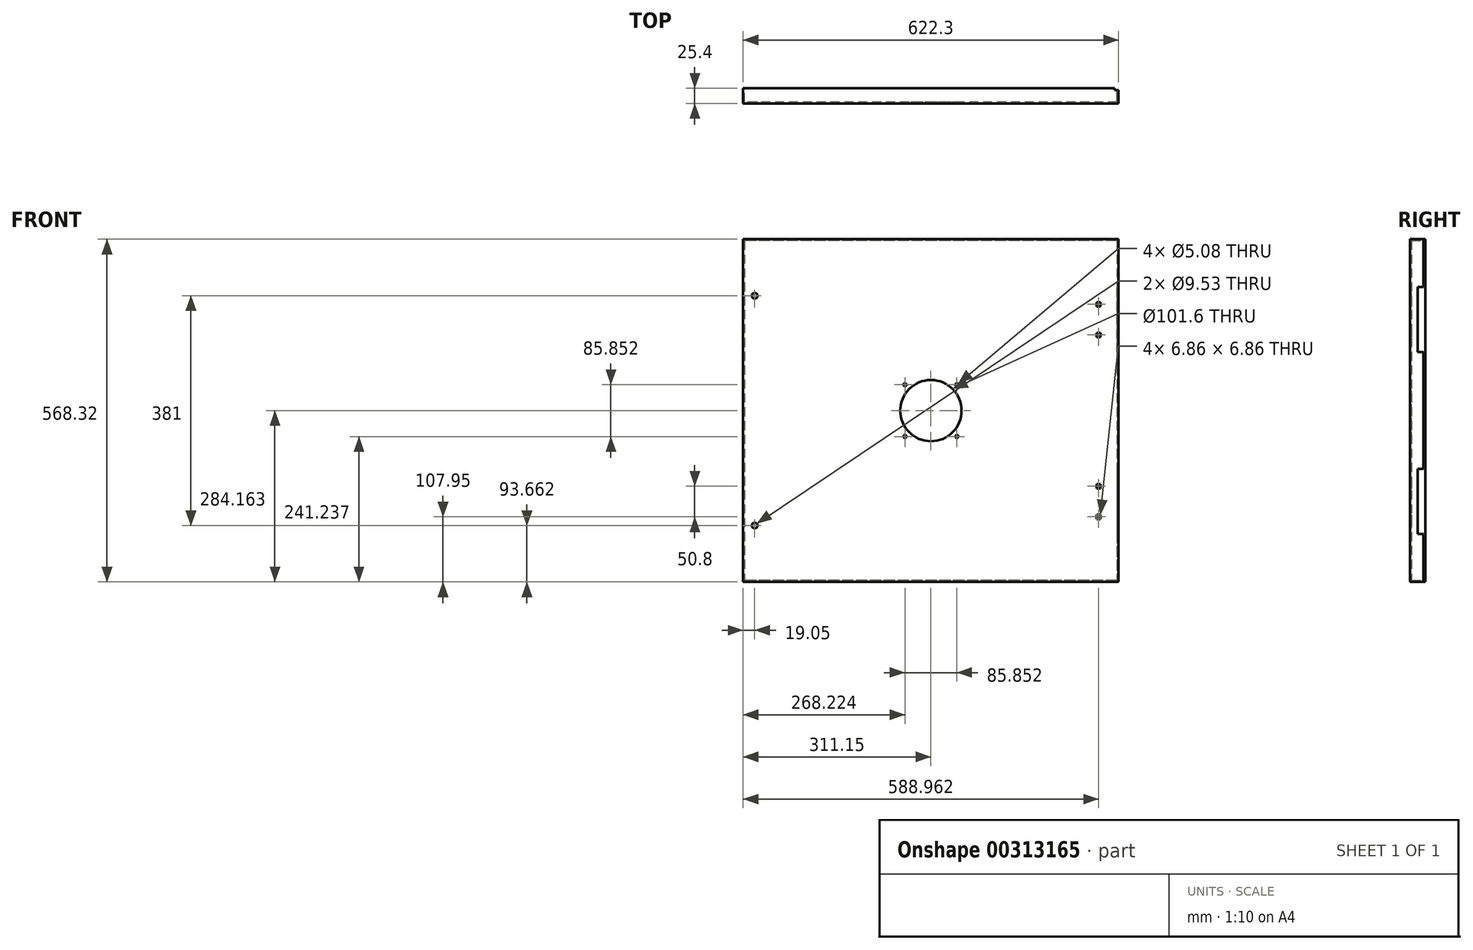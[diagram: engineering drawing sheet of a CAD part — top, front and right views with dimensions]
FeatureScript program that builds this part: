
annotation { "Feature Type Name" : "Feature", "Feature Type Description" : "" }
export const myFeature = defineFeature(function(context is Context, id is Id, definition is map)
    precondition{}
    {
        {
            var Q0;
            Q0=qCreatedBy(makeId("Front.planeOp"),FACE);
            var sketch = newSketch(context, id + "F0", { "sketchPlane" : qUnion([Q0])});
            skLineSegment(sketch, "E0.bottom", {"start": v(311.15, 568.33) * mm, "end": v(-311.15, 568.33) * mm});
            skLineSegment(sketch, "E0.top", {"start": v(311.15, 0) * mm, "end": v(-311.15, 0) * mm});
            skLineSegment(sketch, "E0.left", {"start": v(311.15, 568.32) * mm, "end": v(311.15, 0) * mm});
            skLineSegment(sketch, "E0.right", {"start": v(-311.15, 568.32) * mm, "end": v(-311.15, 0) * mm});
            skCircle(sketch, "E1", {"center": v(-292.1, 474.66) * mm, "radius": 4.76 * mm});
            skCircle(sketch, "E2", {"center": v(-292.1, 93.66) * mm, "radius": 4.76 * mm});
            skCircle(sketch, "E3", {"center": v(277.81, 460.38) * mm, "radius": 3.18 * mm, "construction": true});
            skCircle(sketch, "E4", {"center": v(277.81, 409.58) * mm, "radius": 3.18 * mm, "construction": true});
            skCircle(sketch, "E5", {"center": v(277.81, 158.75) * mm, "radius": 3.18 * mm, "construction": true});
            skCircle(sketch, "E6", {"center": v(277.81, 107.95) * mm, "radius": 3.18 * mm, "construction": true});
            skCircle(sketch, "E7", {"center": v(0, 284.16) * mm, "radius": 50.8 * mm});
            skPoint(sketch, "E7.centerSnap0", {"position": v(-311.15, 284.16) * mm});
            skPoint(sketch, "E7.centerSnap1", {"position": v(0, 568.32) * mm});
            skCircle(sketch, "E8", {"center": v(42.93, 327.09) * mm, "radius": 2.54 * mm});
            skCircle(sketch, "E9", {"center": v(-42.93, 327.09) * mm, "radius": 2.54 * mm});
            skCircle(sketch, "E10", {"center": v(-42.93, 241.24) * mm, "radius": 2.54 * mm});
            skCircle(sketch, "E11", {"center": v(42.93, 241.24) * mm, "radius": 2.54 * mm});
            skLineSegment(sketch, "E12.bottom", {"start": v(281.24, 463.8) * mm, "end": v(274.38, 463.8) * mm});
            skLineSegment(sketch, "E12.top", {"start": v(281.24, 456.95) * mm, "end": v(274.38, 456.95) * mm});
            skLineSegment(sketch, "E12.left", {"start": v(281.24, 463.8) * mm, "end": v(281.24, 456.95) * mm});
            skLineSegment(sketch, "E12.right", {"start": v(274.38, 463.8) * mm, "end": v(274.38, 456.95) * mm});
            skLineSegment(sketch, "E13.bottom", {"start": v(281.24, 413) * mm, "end": v(274.38, 413) * mm});
            skLineSegment(sketch, "E13.top", {"start": v(281.24, 406.15) * mm, "end": v(274.38, 406.15) * mm});
            skLineSegment(sketch, "E13.left", {"start": v(281.24, 413) * mm, "end": v(281.24, 406.15) * mm});
            skLineSegment(sketch, "E13.right", {"start": v(274.38, 413) * mm, "end": v(274.38, 406.15) * mm});
            skLineSegment(sketch, "E14.bottom", {"start": v(281.24, 162.18) * mm, "end": v(274.38, 162.18) * mm});
            skLineSegment(sketch, "E14.top", {"start": v(281.24, 155.32) * mm, "end": v(274.38, 155.32) * mm});
            skLineSegment(sketch, "E14.left", {"start": v(281.24, 162.18) * mm, "end": v(281.24, 155.32) * mm});
            skLineSegment(sketch, "E14.right", {"start": v(274.38, 162.18) * mm, "end": v(274.38, 155.32) * mm});
            skLineSegment(sketch, "E15.bottom", {"start": v(281.24, 111.38) * mm, "end": v(274.38, 111.38) * mm});
            skLineSegment(sketch, "E15.top", {"start": v(281.24, 104.52) * mm, "end": v(274.38, 104.52) * mm});
            skLineSegment(sketch, "E15.left", {"start": v(281.24, 111.38) * mm, "end": v(281.24, 104.52) * mm});
            skLineSegment(sketch, "E15.right", {"start": v(274.38, 111.38) * mm, "end": v(274.38, 104.52) * mm});
            skPoint(sketch, "E15.cornerSnap0", {"position": v(281.24, 158.75) * mm});
            skSolve(sketch);
        }
        {
            var Q0;
            Q0=qSketchRegion(id+"F0",true);
            extrude(context, id + "F1", {"entities" : qUnion([Q0]), "depth" : 25.4 * mm});
        }
        {
            var Q0;
            Q0=makeQuery(id+"F1.opExtrude","CAP_FACE",FACE,{"disambiguationData":[OSD([sQuery(id+"F0.wireOp",EDGE,"E0.bottom"),sQuery(id+"F0.wireOp",EDGE,"E0.top"),sQuery(id+"F0.wireOp",EDGE,"E0.left"),sQuery(id+"F0.wireOp",EDGE,"E0.right"),sQuery(id+"F0.wireOp",EDGE,"DnOeYdpL-yZhG-pMPP-nWlj-HbxDlVvFq81o.bottom"),sQuery(id+"F0.wireOp",EDGE,"DnOeYdpL-yZhG-pMPP-nWlj-HbxDlVvFq81o.top"),sQuery(id+"F0.wireOp",EDGE,"DnOeYdpL-yZhG-pMPP-nWlj-HbxDlVvFq81o.left"),sQuery(id+"F0.wireOp",EDGE,"DnOeYdpL-yZhG-pMPP-nWlj-HbxDlVvFq81o.right"),sQuery(id+"F0.wireOp",EDGE,"xDgMzqlZ-3YCT-1KnM-qA8u-792qYw5lw1JS"),sQuery(id+"F0.wireOp",EDGE,"Mpdr3xRK-0yTI-dkfT-nTdE-cEWg6RnXpa9N"),sQuery(id+"F0.wireOp",EDGE,"UzSud16w-tGWN-ZEeO-kTY7-zgmRVJxoJOe7"),sQuery(id+"F0.wireOp",EDGE,"QdRWkNVw-568D-XgAy-SO4V-4Q89nbcZrelq"),sQuery(id+"F0.wireOp",EDGE,"8aFPr5qc-bRuC-cZr7-87dc-hIFrfZXMsOHR"),sQuery(id+"F0.wireOp",EDGE,"mJVcAo0T-mOHa-Qb8O-DeX9-rnRp2EFAdPQ3"),sQuery(id+"F0.wireOp",EDGE,"58VjJvAl-gczf-lvPp-maZi-m7BX2DlegteS"),sQuery(id+"F0.wireOp",EDGE,"xgLxJu9m-eS83-UV5U-zqJ0-FrWtQ9vBuum0"),sQuery(id+"F0.wireOp",EDGE,"wqzXiebe-RaGP-8YjT-blUU-62aUiCvM27mv"),sQuery(id+"F0.wireOp",EDGE,"zmVhXP7j-02Ai-JLcr-0Ks7-3LBVpZUHfUrI"),sQuery(id+"F0.wireOp",EDGE,"BW3LuwXz-W35X-CTuh-aFvS-jlk6UlRIqyyT"),sQuery(id+"F0.wireOp",EDGE,"GNJOQj1j-LiCZ-vYCN-EfaB-cui9jyFQZn0N"),sQuery(id+"F0.wireOp",EDGE,"da7037a2-8101-4e2d-bd9b-c90a86b3fb6c.1.0.1"),sQuery(id+"F0.wireOp",EDGE,"da7037a2-8101-4e2d-bd9b-c90a86b3fb6c.1.0.2"),sQuery(id+"F0.wireOp",EDGE,"da7037a2-8101-4e2d-bd9b-c90a86b3fb6c.1.0.3"),sQuery(id+"F0.wireOp",EDGE,"da7037a2-8101-4e2d-bd9b-c90a86b3fb6c.1.0.4"),sQuery(id+"F0.wireOp",EDGE,"da7037a2-8101-4e2d-bd9b-c90a86b3fb6c.1.0.5"),sQuery(id+"F0.wireOp",EDGE,"da7037a2-8101-4e2d-bd9b-c90a86b3fb6c.1.0.6"),sQuery(id+"F0.wireOp",EDGE,"da7037a2-8101-4e2d-bd9b-c90a86b3fb6c.1.0.7"),sQuery(id+"F0.wireOp",EDGE,"da7037a2-8101-4e2d-bd9b-c90a86b3fb6c.1.0.8"),sQuery(id+"F0.wireOp",EDGE,"da7037a2-8101-4e2d-bd9b-c90a86b3fb6c.1.0.9"),sQuery(id+"F0.wireOp",EDGE,"da7037a2-8101-4e2d-bd9b-c90a86b3fb6c.1.0.10"),sQuery(id+"F0.wireOp",EDGE,"da7037a2-8101-4e2d-bd9b-c90a86b3fb6c.1.0.11"),sQuery(id+"F0.wireOp",EDGE,"da7037a2-8101-4e2d-bd9b-c90a86b3fb6c.1.0.12"),sQuery(id+"F0.wireOp",EDGE,"da7037a2-8101-4e2d-bd9b-c90a86b3fb6c.1.0.13"),sQuery(id+"F0.wireOp",EDGE,"da7037a2-8101-4e2d-bd9b-c90a86b3fb6c.1.0.14"),sQuery(id+"F0.wireOp",EDGE,"da7037a2-8101-4e2d-bd9b-c90a86b3fb6c.1.0.15"),sQuery(id+"F0.wireOp",EDGE,"da7037a2-8101-4e2d-bd9b-c90a86b3fb6c.1.0.16")])],"isStart":true});
            shell(context, id + "F2", {"entities" : qUnion([Q0]), "thickness" : 2.54 * mm});
        }
        {
            var Q0;
            Q0=makeQuery(id+"F2.opShell","OFFSET_FACE",FACE,{"disambiguationData":[OSD([sQuery(id+"F0.wireOp",EDGE,"E0.top")])]});
            var sketch = newSketch(context, id + "F3", { "sketchPlane" : qUnion([Q0])});
            skLineSegment(sketch, "E16.bottom", {"start": v(308.61, 0) * mm, "end": v(-308.61, 0) * mm});
            skLineSegment(sketch, "E16.top", {"start": v(308.61, -22.86) * mm, "end": v(-308.61, -22.86) * mm});
            skLineSegment(sketch, "E16.left", {"start": v(308.61, 0) * mm, "end": v(308.61, -22.86) * mm});
            skLineSegment(sketch, "E16.right", {"start": v(-308.61, 0) * mm, "end": v(-308.61, -22.86) * mm});
            skSolve(sketch);
        }
        {
            var Q0;
            Q0 = qSketchRegion(id + "F3", true);
            var Q1;
            Q1=makeQuery(id+"F2.opShell","OFFSET_FACE",FACE,{"disambiguationData":[OSD([sQuery(id+"F0.wireOp",EDGE,"E0.bottom")])]});
            extrude(context, id + "F4", {"entities" : qUnion([Q0]), "operationType" : NewBodyOperationType.REMOVE, "endBound" : BoundingType.UP_TO_SURFACE, "endBoundEntityFace" : qUnion([Q1]), "depth" : 25.4 * mm});
        }
        {
            var Q0;
            Q0=makeQuery(id+"F1.opExtrude","SWEPT_FACE",FACE,{"disambiguationData":[OSD([sQuery(id+"F0.wireOp",EDGE,"E0.bottom")])]});
            var sketch = newSketch(context, id + "F5", { "sketchPlane" : qUnion([Q0])});
            skLineSegment(sketch, "E17", {"start": v(304.8, 0) * mm, "end": v(304.8, -3.18) * mm});
            skLineSegment(sketch, "E18", {"start": v(304.8, -3.18) * mm, "end": v(311.15, -3.18) * mm});
            skLineSegment(sketch, "E19", {"start": v(311.15, -3.18) * mm, "end": v(311.15, 0) * mm});
            skLineSegment(sketch, "E20", {"start": v(304.8, 0) * mm, "end": v(311.15, 0) * mm});
            skSolve(sketch);
        }
        {
            var Q0;
            Q0 = qSketchRegion(id + "F5", true);
            extrude(context, id + "F6", {"entities" : qUnion([Q0]), "operationType" : NewBodyOperationType.REMOVE, "endBound" : BoundingType.THROUGH_ALL, "oppositeDirection" : true, "depth" : 25.4 * mm});
        }
        {
            var Q0;
            Q0=makeQuery(id+"F1.opExtrude","SWEPT_FACE",FACE,{"disambiguationData":[OSD([sQuery(id+"F0.wireOp",EDGE,"E0.left")])]});
            var sketch = newSketch(context, id + "F7", { "sketchPlane" : qUnion([Q0])});
            skLineSegment(sketch, "E21.bottom", {"start": v(0, 488.95) * mm, "end": v(-12.7, 488.95) * mm});
            skLineSegment(sketch, "E21.top", {"start": v(0, 381) * mm, "end": v(-12.7, 381) * mm});
            skLineSegment(sketch, "E21.left", {"start": v(0, 488.95) * mm, "end": v(0, 381) * mm});
            skLineSegment(sketch, "E21.right", {"start": v(-12.7, 488.95) * mm, "end": v(-12.7, 381) * mm});
            skLineSegment(sketch, "E22.bottom", {"start": v(0, 79.37) * mm, "end": v(-12.7, 79.37) * mm});
            skLineSegment(sketch, "E22.top", {"start": v(0, 187.32) * mm, "end": v(-12.7, 187.32) * mm});
            skLineSegment(sketch, "E22.left", {"start": v(0, 79.37) * mm, "end": v(0, 187.32) * mm});
            skLineSegment(sketch, "E22.right", {"start": v(-12.7, 79.37) * mm, "end": v(-12.7, 187.32) * mm});
            skPoint(sketch, "E23", {"position": v(-12.7, 434.98) * mm});
            skPoint(sketch, "E24", {"position": v(-12.7, 133.35) * mm});
            skSolve(sketch);
        }
        {
            var Q0;
            Q0 = qSketchRegion(id + "F7", true);
            extrude(context, id + "F8", {"entities" : qUnion([Q0]), "operationType" : NewBodyOperationType.REMOVE, "endBound" : BoundingType.UP_TO_NEXT, "oppositeDirection" : true, "depth" : 25.4 * mm});
        }
    });
